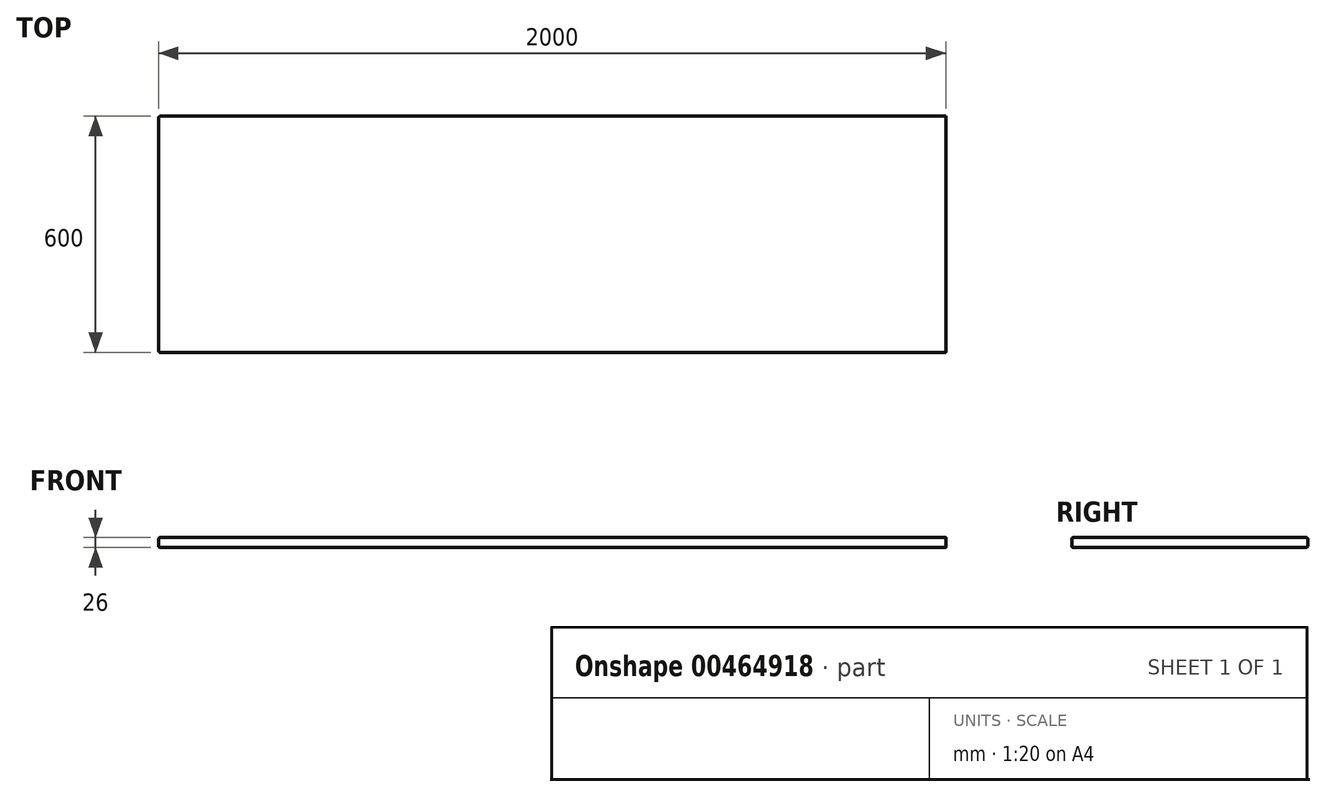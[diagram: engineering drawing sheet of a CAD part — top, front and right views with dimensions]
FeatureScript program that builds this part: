
annotation { "Feature Type Name" : "Feature", "Feature Type Description" : "" }
export const myFeature = defineFeature(function(context is Context, id is Id, definition is map)
    precondition{}
    {
        {
            var Q0;
            Q0=qCreatedBy(makeId("Top.planeOp"),FACE);
            var sketch = newSketch(context, id + "F0", { "sketchPlane" : qUnion([Q0])});
            skLineSegment(sketch, "E0.bottom", {"start": v(-1100, -300) * mm, "end": v(1100, -300) * mm});
            skLineSegment(sketch, "E0.top", {"start": v(-1100, 300) * mm, "end": v(1100, 300) * mm});
            skLineSegment(sketch, "E0.left", {"start": v(-1100, -300) * mm, "end": v(-1100, 300) * mm});
            skLineSegment(sketch, "E0.right", {"start": v(1100, -300) * mm, "end": v(1100, 300) * mm});
            skPoint(sketch, "E0.middle", {"position": v(0, 0) * mm});
            skLineSegment(sketch, "E1", {"start": v(-1100, 0) * mm, "end": v(1100, 0) * mm, "construction": true});
            skSolve(sketch);
        }
        {
            var Q0;
            Q0=makeQuery(id+"F0.imprint","IMPRINT",FACE,{"disambiguationData":[TD([[makeQuery(id+"F0.imprint","IMPRINT",EDGE,{"derivedFrom":sQuery(id+"F0.wireOp",EDGE,"E0.bottom")}),1.0]])]});
            extrude(context, id + "F1", {"entities" : qUnion([Q0]), "depth" : 26 * mm, "offsetDistance" : 25 * mm});
        }
        {
            var Q0;
            Q0=makeQuery(id+"F1.opExtrude","CAP_FACE",FACE,{"disambiguationData":[OSD([sQuery(id+"F0.wireOp",EDGE,"E0.bottom"),sQuery(id+"F0.wireOp",EDGE,"E0.top"),sQuery(id+"F0.wireOp",EDGE,"E0.left"),sQuery(id+"F0.wireOp",EDGE,"E0.right")])],"isStart":false});
            var Q1;
            Q1=makeQuery(id+"F1.opExtrude","CAP_FACE",FACE,{"disambiguationData":[OSD([sQuery(id+"F0.wireOp",EDGE,"E0.bottom"),sQuery(id+"F0.wireOp",EDGE,"E0.top"),sQuery(id+"F0.wireOp",EDGE,"E0.left"),sQuery(id+"F0.wireOp",EDGE,"E0.right")])],"isStart":true});
            var Q2;
            Q2=makeQuery(id+"F1.opExtrude","SWEPT_EDGE",EDGE,{"disambiguationData":[OSD([sQuery(id+"F0.wireOp",EDGE,"E0.bottom"),sQuery(id+"F0.wireOp",EDGE,"E0.left")])]});
            var Q3;
            Q3=makeQuery(id+"F1.opExtrude","SWEPT_EDGE",EDGE,{"disambiguationData":[OSD([sQuery(id+"F0.wireOp",EDGE,"E0.top"),sQuery(id+"F0.wireOp",EDGE,"E0.left")])]});
            var Q4;
            Q4=makeQuery(id+"F1.opExtrude","SWEPT_EDGE",EDGE,{"disambiguationData":[OSD([sQuery(id+"F0.wireOp",EDGE,"E0.top"),sQuery(id+"F0.wireOp",EDGE,"E0.right")])]});
            var Q5;
            Q5=makeQuery(id+"F1.opExtrude","SWEPT_EDGE",EDGE,{"disambiguationData":[OSD([sQuery(id+"F0.wireOp",EDGE,"E0.bottom"),sQuery(id+"F0.wireOp",EDGE,"E0.right")])]});
            fillet(context, id + "F2", {"entities" : qUnion([Q0, Q1, Q2, Q3, Q4, Q5]), "radius" : 5 * mm, "tangentPropagation" : true, "allowEdgeOverflow" : false});
        }
        {
            var Q0;
            Q0=makeQuery(id+"F1.opExtrude","SWEPT_FACE",FACE,{"disambiguationData":[OSD([sQuery(id+"F0.wireOp",EDGE,"E0.right")])]});
            var sketch = newSketch(context, id + "F3", { "sketchPlane" : qUnion([Q0])});
            skLineSegment(sketch, "E2.bottom", {"start": v(-300, 26) * mm, "end": v(300, 26) * mm});
            skLineSegment(sketch, "E2.top", {"start": v(-300, 0) * mm, "end": v(300, 0) * mm});
            skLineSegment(sketch, "E2.left", {"start": v(-300, 26) * mm, "end": v(-300, 0) * mm});
            skLineSegment(sketch, "E2.right", {"start": v(300, 26) * mm, "end": v(300, 0) * mm});
            skSolve(sketch);
        }
        {
            var Q0;
            Q0 = qSketchRegion(id + "F3", true);
            extrude(context, id + "F4", {"entities" : qUnion([Q0]), "operationType" : NewBodyOperationType.REMOVE, "oppositeDirection" : true, "depth" : 200 * mm, "offsetDistance" : 25 * mm});
        }
    });
